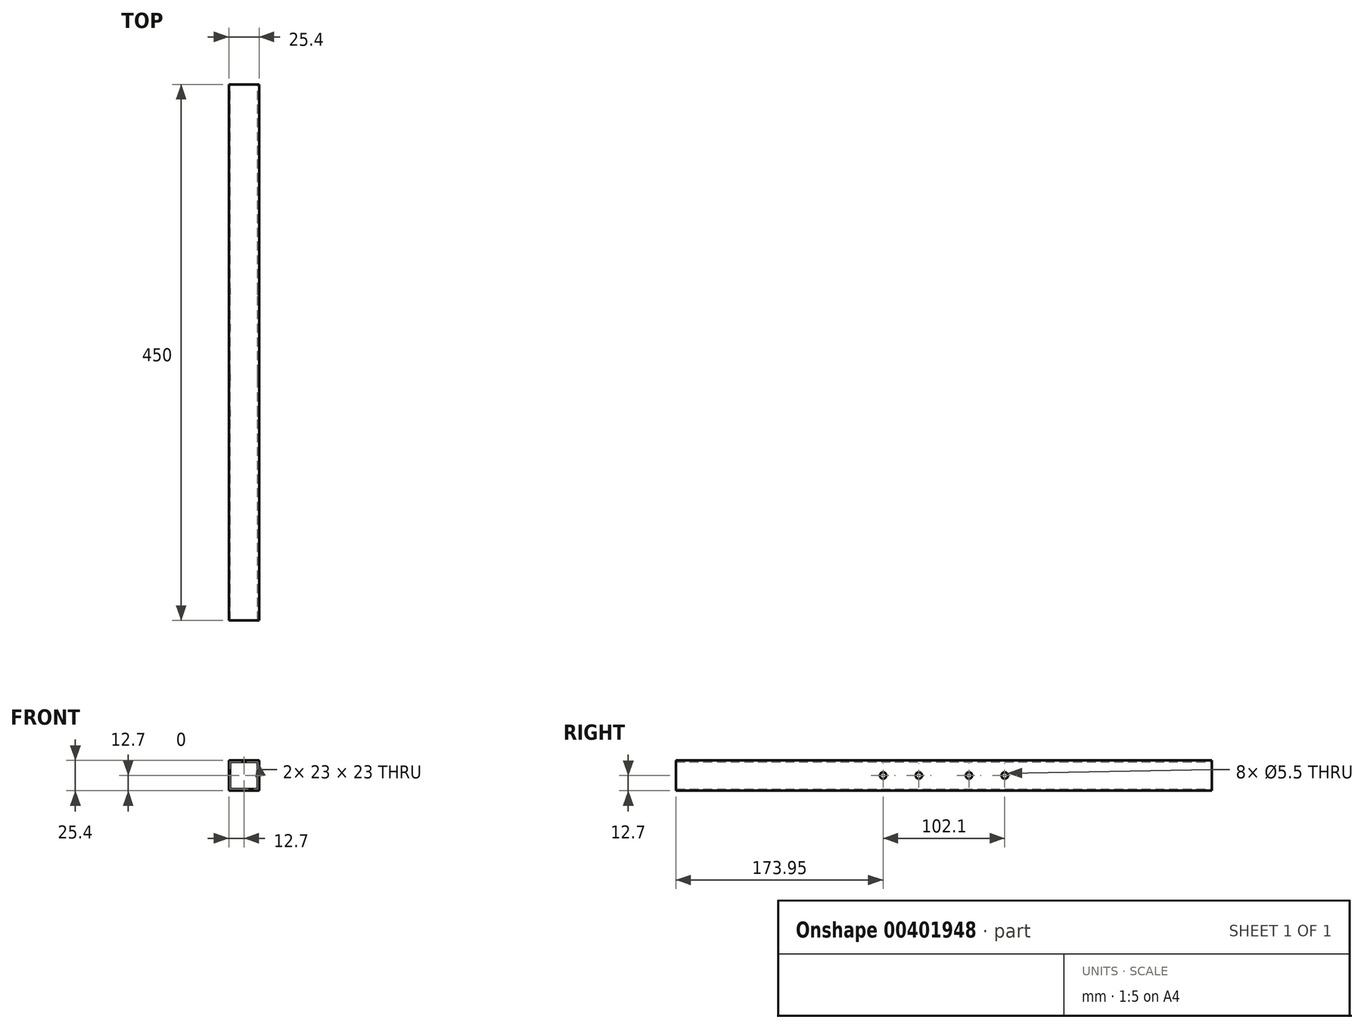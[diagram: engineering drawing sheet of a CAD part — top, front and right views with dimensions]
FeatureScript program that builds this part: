
annotation { "Feature Type Name" : "Feature", "Feature Type Description" : "" }
export const myFeature = defineFeature(function(context is Context, id is Id, definition is map)
    precondition{}
    {
        {
            var Q0;
            Q0=qCreatedBy(makeId("Front.planeOp"),FACE);
            var sketch = newSketch(context, id + "F0", { "sketchPlane" : qUnion([Q0])});
            skLineSegment(sketch, "E0.bottom", {"start": v(-12.7, 12.7) * mm, "end": v(12.7, 12.7) * mm});
            skLineSegment(sketch, "E0.top", {"start": v(-12.7, -12.7) * mm, "end": v(12.7, -12.7) * mm});
            skLineSegment(sketch, "E0.left", {"start": v(-12.7, 12.7) * mm, "end": v(-12.7, -12.7) * mm});
            skLineSegment(sketch, "E0.right", {"start": v(12.7, 12.7) * mm, "end": v(12.7, -12.7) * mm});
            skLineSegment(sketch, "E1", {"start": v(0, 0) * mm, "end": v(0, 12.7) * mm, "construction": true});
            skLineSegment(sketch, "E2", {"start": v(0, 0) * mm, "end": v(-12.7, 0) * mm, "construction": true});
            skLineSegment(sketch, "E3.0", {"start": v(-11.5, -11.5) * mm, "end": v(11.5, -11.5) * mm});
            skLineSegment(sketch, "E3.1", {"start": v(-11.5, 11.5) * mm, "end": v(-11.5, -11.5) * mm});
            skLineSegment(sketch, "E3.2", {"start": v(-11.5, 11.5) * mm, "end": v(11.5, 11.5) * mm});
            skLineSegment(sketch, "E3.3", {"start": v(11.5, 11.5) * mm, "end": v(11.5, -11.5) * mm});
            skSolve(sketch);
        }
        {
            var Q0;
            Q0 = qSketchRegion(id + "F0", true);
            var Q1;
            Q1 = qConstructionFilter(qBodyType(qCreatedBy(id + "F0" ,EDGE), BodyType.WIRE), ConstructionObject.NO);
            extrude(context, id + "F1", {"entities" : qUnion([Q0]), "surfaceEntities" : qUnion([Q1]), "endBound" : BoundingType.SYMMETRIC, "depth" : 450 * mm});
        }
        {
            var Q0;
            Q0 = qSketchRegion(id + "F0", true);
            extrude(context, id + "F2", {"entities" : qUnion([Q0]), "endBound" : BoundingType.SYMMETRIC, "depth" : 450 * mm});
        }
        {
            var Q0;
            Q0=makeQuery(id+"F2.opExtrude","SWEPT_FACE",FACE,{"disambiguationData":[OSD([sQuery(id+"F0.wireOp",EDGE,"E0.right")])]});
            var sketch = newSketch(context, id + "F3", { "sketchPlane" : qUnion([Q0])});
            skPoint(sketch, "E4", {"position": v(-21.05, 0) * mm});
            skPoint(sketch, "E5", {"position": v(-51.05, 0) * mm});
            skLineSegment(sketch, "E6", {"start": v(0, 0) * mm, "end": v(0, 36.04) * mm, "construction": true});
            skPoint(sketch, "E7.MirrorP", {"position": v(21.05, 0) * mm});
            skPoint(sketch, "E8.MirrorP", {"position": v(51.05, 0) * mm});
            skSolve(sketch);
        }
        {
            var Q0;
            Q0=sQuery(id+"F3.wireOp",VERTEX,"E5");
            var Q1;
            Q1=sQuery(id+"F3.wireOp",VERTEX,"E4");
            var Q2;
            Q2=sQuery(id+"F3.wireOp",VERTEX,"E7.MirrorP");
            var Q3;
            Q3=sQuery(id+"F3.wireOp",VERTEX,"E8.MirrorP");
            var Q4;
            Q4=makeQuery(id+"F2.opExtrude","SWEPT_BODY",BODY,{"disambiguationData":[OSD([sQuery(id+"F0.wireOp",EDGE,"E0.bottom"),sQuery(id+"F0.wireOp",EDGE,"E0.top"),sQuery(id+"F0.wireOp",EDGE,"E0.left"),sQuery(id+"F0.wireOp",EDGE,"E0.right"),sQuery(id+"F0.wireOp",EDGE,"E3.0"),sQuery(id+"F0.wireOp",EDGE,"E3.1"),sQuery(id+"F0.wireOp",EDGE,"E3.2"),sQuery(id+"F0.wireOp",EDGE,"E3.3")])]});
            hole(context, id + "F4", {"style" : HoleStyle.SIMPLE, "endStyle" : HoleEndStyle.THROUGH, "holeDiameter" : 5.5 * mm, "isTappedThrough" : true, "tappedDepth" : 12 * mm, "tapClearance" : 3, "locations" : qUnion([Q0, Q1, Q2, Q3]), "scope" : qUnion([Q4])});
        }
    });
